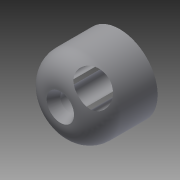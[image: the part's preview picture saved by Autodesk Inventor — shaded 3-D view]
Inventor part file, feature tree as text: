
AUTODESK INVENTOR PART (.ipt)
format: ipt  version: 2015 (Build 190159000, 159)  size: 132,608 bytes
history: native  units: in
note: dims shown in document units (in); Inventor stores cm internally (conversion verified against a paired STEP export)
features: extrude x3, sketch x3, fillet x1, chamfer x1
ambient origin geometry x8: Origin, YZ Plane, XZ Plane, XY Plane, X Axis, Y Axis, Z Axis, Center Point
bodies: Solid1 (feature_tree)
feature tree (8):
  extrude  "Extrusion1"  Depth=0.5in
  extrude  "Extrusion6"  Depth=0.1065in
  fillet  "Fillet2"  Radius=0.1065in
  extrude  "Extrusion7"  Depth=0.3125in TaperAngle=0.0deg
  chamfer  "Chamfer1"  Distance=0.3125in
  sketch  "Sketch1"  dims[d0=0.5in d1=0.0in d12=0.2402in]
  sketch  "Sketch7"  dims[d13=0.1065in d14=0.1065in d15=0.1065in]
  sketch  "Sketch8"  dims[d16=0.1065in d17=0.3125in d18=0.0in d19=0.3125in d21=0.25in d22=1.5in d23=0.0in d24=0.0625in d25=0.125in d26=45.0deg]
